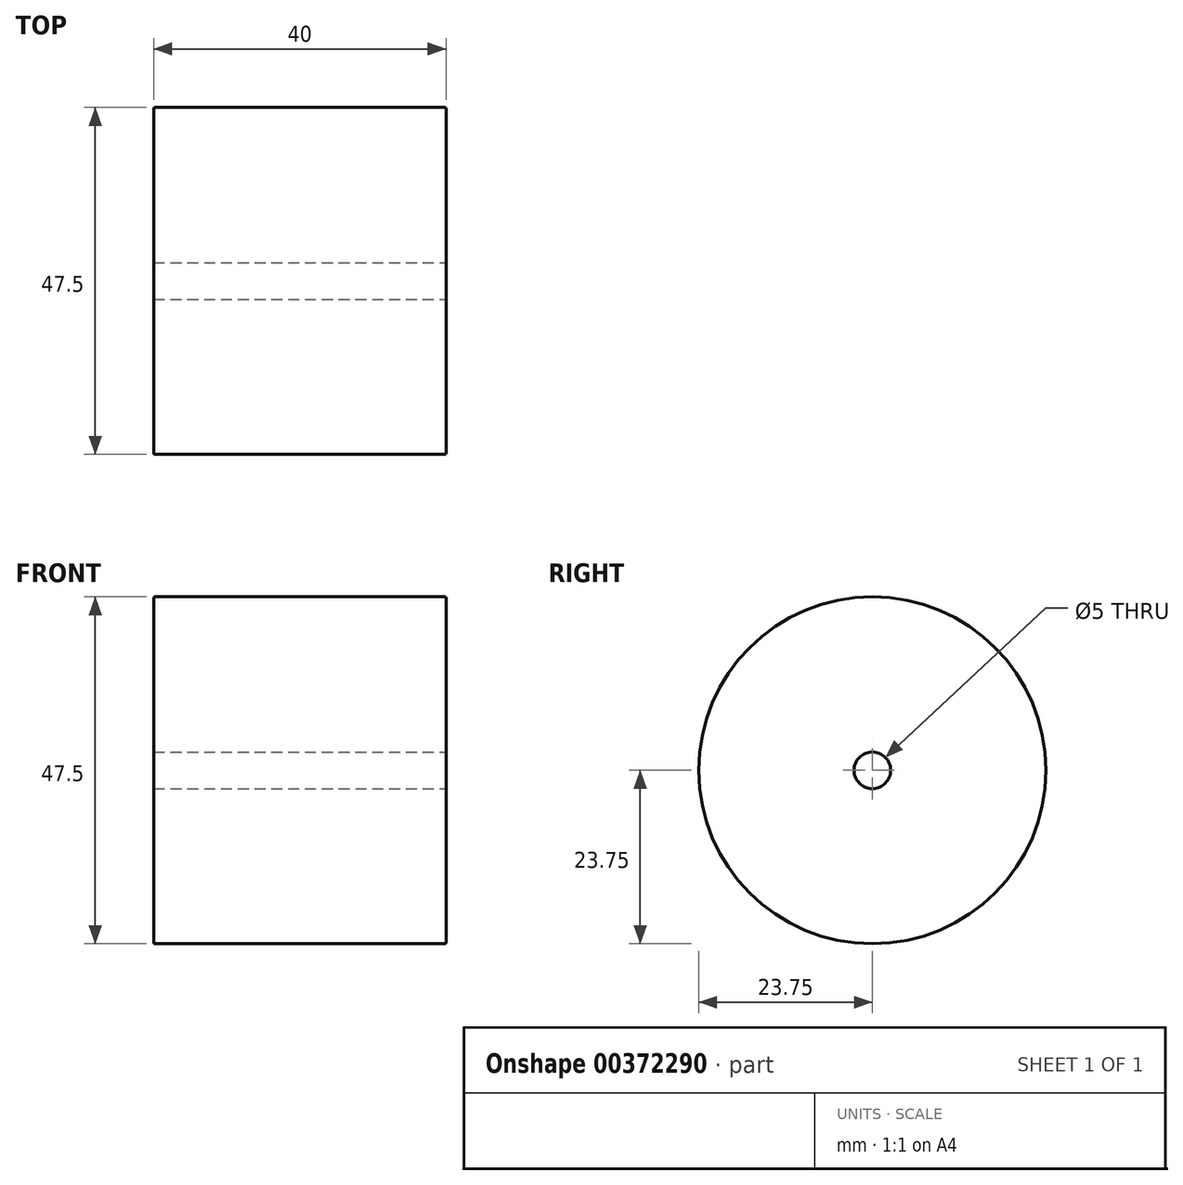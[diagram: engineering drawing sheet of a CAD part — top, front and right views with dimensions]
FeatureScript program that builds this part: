
annotation { "Feature Type Name" : "Feature", "Feature Type Description" : "" }
export const myFeature = defineFeature(function(context is Context, id is Id, definition is map)
    precondition{}
    {
        {
            var Q0;
            Q0=qCreatedBy(makeId("Right.planeOp"),FACE);
            var sketch = newSketch(context, id + "F0", { "sketchPlane" : qUnion([Q0])});
            skCircle(sketch, "E0", {"center": v(0, 0) * mm, "radius": 23.75 * mm});
            skSolve(sketch);
        }
        {
            var Q0;
            Q0=makeQuery(id+"F0.imprint","IMPRINT",FACE,{"disambiguationData":[TD([[makeQuery(id+"F0.imprint","IMPRINT",EDGE,{"derivedFrom":sQuery(id+"F0.wireOp",EDGE,"E0")}),1.0]])]});
            extrude(context, id + "F1", {"entities" : qUnion([Q0]), "depth" : 40 * mm, "symmetric" : true});
        }
        {
            var Q0;
            Q0=makeQuery(id+"F1.opExtrude","CAP_FACE",FACE,{"disambiguationData":[OSD([sQuery(id+"F0.wireOp",EDGE,"E0")])],"isStart":false});
            var sketch = newSketch(context, id + "F2", { "sketchPlane" : qUnion([Q0])});
            skCircle(sketch, "E1", {"center": v(0, 0) * mm, "radius": 2.5 * mm});
            skSolve(sketch);
        }
        {
            var Q0;
            Q0=qSketchRegion(id+"F2",true);
            extrude(context, id + "F3", {"entities" : qUnion([Q0]), "operationType" : NewBodyOperationType.REMOVE, "endBound" : BoundingType.THROUGH_ALL, "oppositeDirection" : true, "depth" : 25 * mm});
        }
        {
            var Q0;
            Q0=makeQuery(id+"F1.opExtrude","CAP_EDGE",EDGE,{"disambiguationData":[OSD([sQuery(id+"F0.wireOp",EDGE,"E0")])],"isStart":false});
            var Q1;
            Q1=makeQuery(id+"F1.opExtrude","CAP_EDGE",EDGE,{"disambiguationData":[OSD([sQuery(id+"F0.wireOp",EDGE,"E0")])],"isStart":true});
            fillet(context, id + "F4", {"entities" : qUnion([Q0, Q1]), "radius" : 0.2 * mm, "tangentPropagation" : true, "allowEdgeOverflow" : false});
        }
    });
